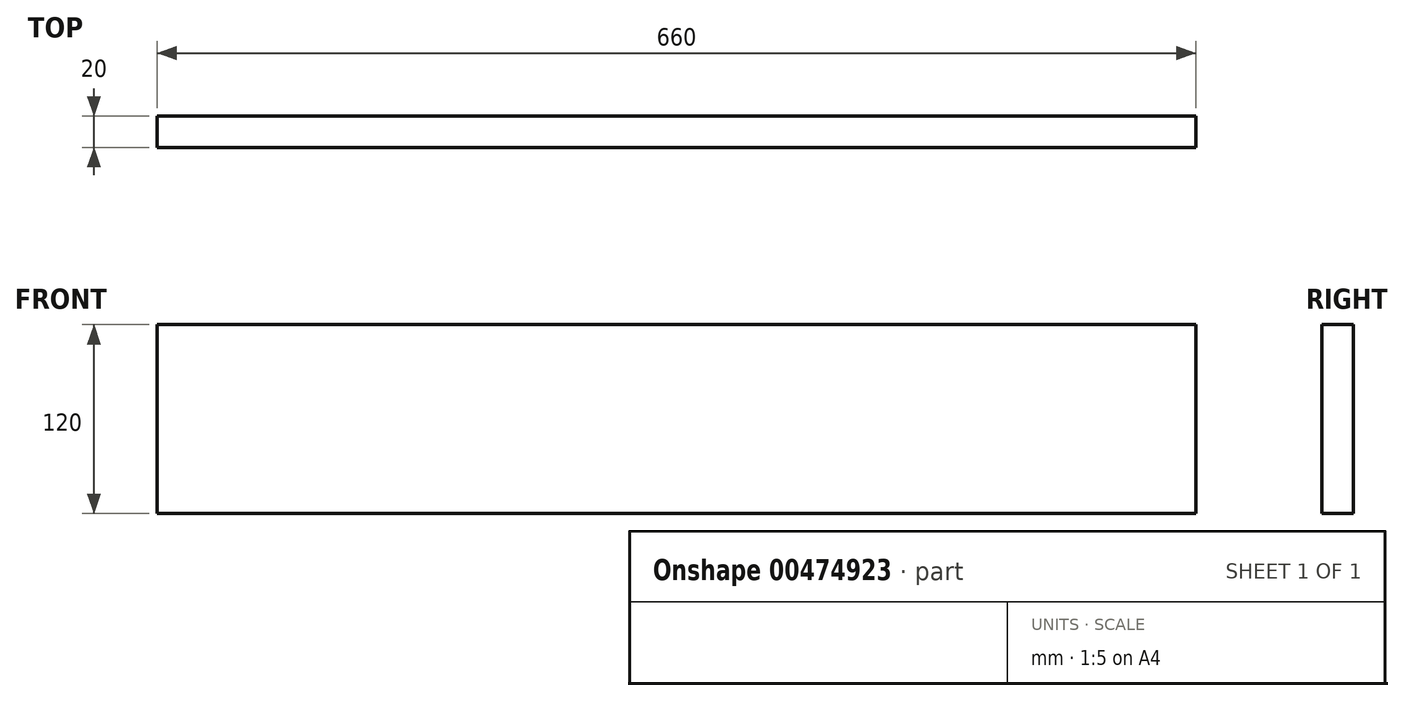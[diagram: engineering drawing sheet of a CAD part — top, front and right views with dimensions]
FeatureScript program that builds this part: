
annotation { "Feature Type Name" : "Feature", "Feature Type Description" : "" }
export const myFeature = defineFeature(function(context is Context, id is Id, definition is map)
    precondition{}
    {
        {
            var Q0;
            Q0=qCreatedBy(makeId("Front.planeOp"),FACE);
            var sketch = newSketch(context, id + "F0", { "sketchPlane" : qUnion([Q0])});
            skLineSegment(sketch, "E0.bottom", {"start": v(-279.26, -109.92) * mm, "end": v(380.74, -109.92) * mm});
            skLineSegment(sketch, "E0.top", {"start": v(-279.26, -229.92) * mm, "end": v(380.74, -229.92) * mm});
            skLineSegment(sketch, "E0.left", {"start": v(-279.26, -109.92) * mm, "end": v(-279.26, -229.92) * mm});
            skLineSegment(sketch, "E0.right", {"start": v(380.74, -109.92) * mm, "end": v(380.74, -229.92) * mm});
            skPoint(sketch, "E1.endSnap0", {"position": v(50.74, -109.92) * mm});
            skSolve(sketch);
        }
        {
            var Q0;
            Q0=makeQuery(id+"F0.imprint","IMPRINT",FACE,{"disambiguationData":[TD([[makeQuery(id+"F0.imprint","IMPRINT",EDGE,{"derivedFrom":sQuery(id+"F0.wireOp",EDGE,"E0.bottom")}),-1.0]])]});
            extrude(context, id + "F1", {"entities" : qUnion([Q0]), "depth" : 20 * mm, "offsetDistance" : 25 * mm});
        }
    });
